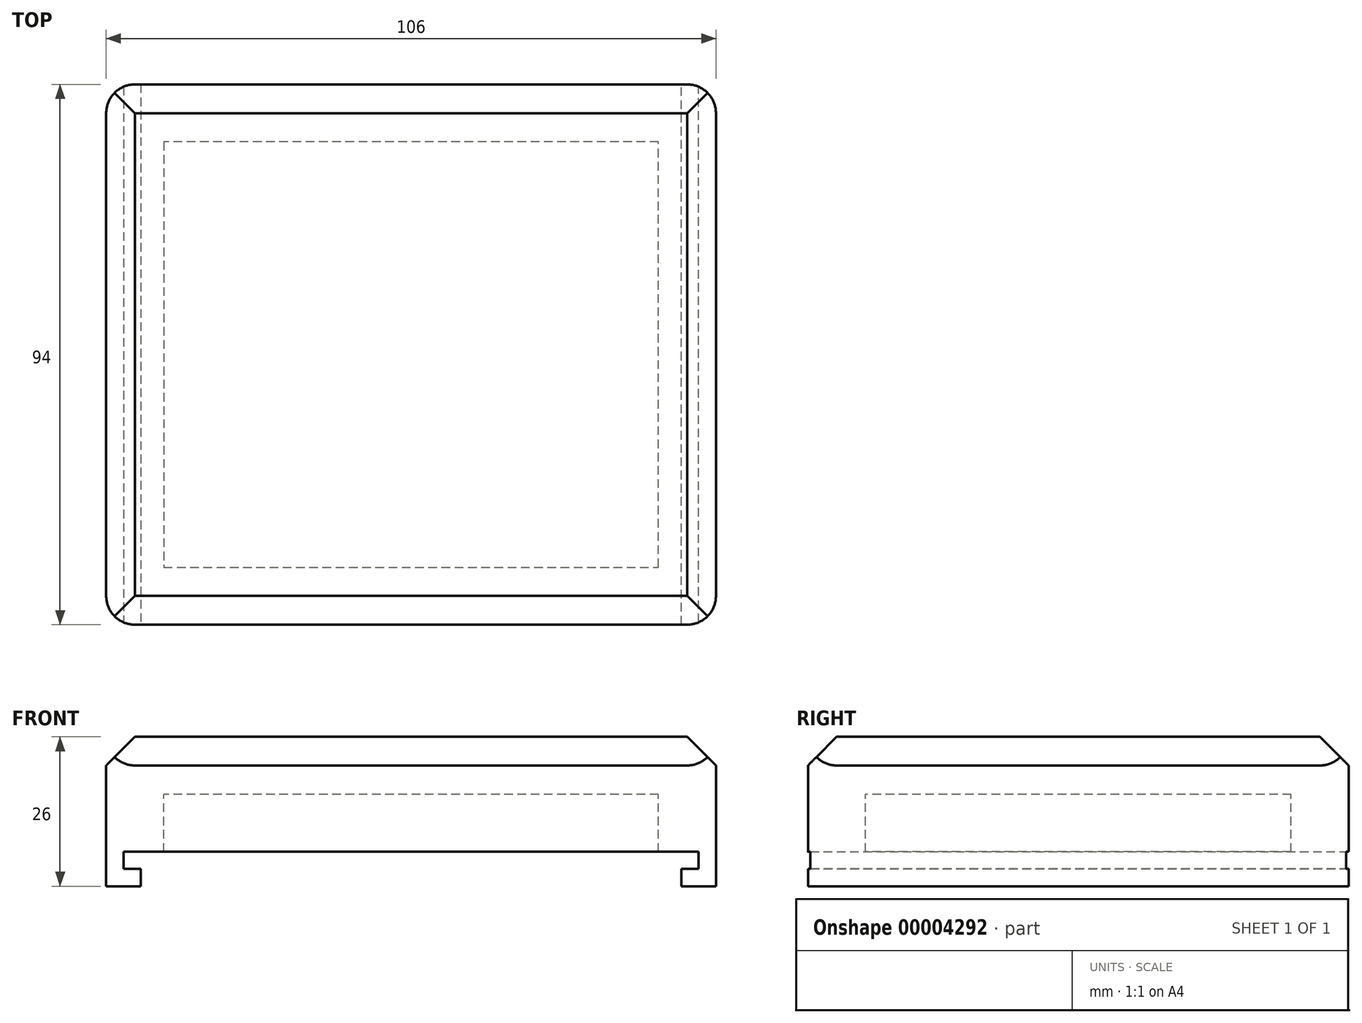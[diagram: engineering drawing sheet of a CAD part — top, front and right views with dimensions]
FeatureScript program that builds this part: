
annotation { "Feature Type Name" : "Feature", "Feature Type Description" : "" }
export const myFeature = defineFeature(function(context is Context, id is Id, definition is map)
    precondition{}
    {
        {
            var Q0;
            Q0=qCreatedBy(makeId("Top.planeOp"),FACE);
            var sketch = newSketch(context, id + "F0", { "sketchPlane" : qUnion([Q0])});
            skLineSegment(sketch, "E0", {"start": v(-102.5, 83.2) * mm, "end": v(-208.5, 83.2) * mm});
            skLineSegment(sketch, "E1", {"start": v(-208.5, 83.2) * mm, "end": v(-208.5, -10.8) * mm});
            skLineSegment(sketch, "E2", {"start": v(-208.5, -10.8) * mm, "end": v(-102.5, -10.8) * mm});
            skLineSegment(sketch, "E3", {"start": v(-102.5, -10.8) * mm, "end": v(-102.5, 83.2) * mm});
            skSolve(sketch);
        }
        {
            var Q0;
            Q0=makeQuery(id+"F0.imprint","IMPRINT",FACE,{"disambiguationData":[TD([[makeQuery(id+"F0.imprint","IMPRINT",EDGE,{"derivedFrom":sQuery(id+"F0.wireOp",EDGE,"E0")}),1.0]])]});
            extrude(context, id + "F1", {"entities" : qUnion([Q0]), "depth" : 10 * mm});
        }
        {
            var Q0;
            Q0=makeQuery(id+"F1.opExtrude","CAP_FACE",FACE,{"disambiguationData":[OSD([sQuery(id+"F0.wireOp",EDGE,"E0"),sQuery(id+"F0.wireOp",EDGE,"E1"),sQuery(id+"F0.wireOp",EDGE,"E2"),sQuery(id+"F0.wireOp",EDGE,"E3")])],"isStart":true});
            var sketch = newSketch(context, id + "F2", { "sketchPlane" : qUnion([Q0])});
            skSolve(sketch);
        }
        {
            var Q0;
            Q0=makeQuery(id+"F2.imprint","IMPRINT",FACE,{"disambiguationData":[TD([[makeQuery(id+"F2.imprint","IMPRINT",EDGE,{"derivedFrom":makeQuery(id+"F1.opExtrude","CAP_EDGE",EDGE,{"disambiguationData":[OSD([sQuery(id+"F0.wireOp",EDGE,"E0")])],"isStart":true})}),-1.0]])]});
            var sketch = newSketch(context, id + "F3", { "sketchPlane" : qUnion([Q0])});
            skLineSegment(sketch, "E4.0", {"start": v(-198.5, -73.2) * mm, "end": v(-198.5, 0.8) * mm});
            skLineSegment(sketch, "E4.1", {"start": v(-112.5, -73.2) * mm, "end": v(-198.5, -73.2) * mm});
            skLineSegment(sketch, "E4.2", {"start": v(-112.5, 0.8) * mm, "end": v(-112.5, -73.2) * mm});
            skLineSegment(sketch, "E4.3", {"start": v(-198.5, 0.8) * mm, "end": v(-112.5, 0.8) * mm});
            skSolve(sketch);
        }
        {
            var Q0;
            Q0=makeQuery(id+"F3.imprint","IMPRINT",FACE,{"disambiguationData":[TD([[makeQuery(id+"F3.imprint","IMPRINT",EDGE,{"derivedFrom":sQuery(id+"F3.wireOp",EDGE,"E4.0")}),1.0]])]});
            extrude(context, id + "F4", {"entities" : qUnion([Q0]), "operationType" : NewBodyOperationType.ADD, "depth" : 10 * mm});
        }
        {
            var Q0;
            Q0=makeQuery(id+"F4.opExtrude","CAP_FACE",FACE,{"disambiguationData":[OSD([sQuery(id+"F0.wireOp",EDGE,"E0"),sQuery(id+"F0.wireOp",EDGE,"E1"),sQuery(id+"F0.wireOp",EDGE,"E2"),sQuery(id+"F0.wireOp",EDGE,"E3"),sQuery(id+"F3.wireOp",EDGE,"E4.0"),sQuery(id+"F3.wireOp",EDGE,"E4.1"),sQuery(id+"F3.wireOp",EDGE,"E4.2"),sQuery(id+"F3.wireOp",EDGE,"E4.3")])],"isStart":false});
            var sketch = newSketch(context, id + "F5", { "sketchPlane" : qUnion([Q0])});
            skLineSegment(sketch, "E5.0", {"start": v(-205.5, -83.2) * mm, "end": v(-205.5, 10.8) * mm});
            skLineSegment(sketch, "E6.0", {"start": v(-105.5, 10.8) * mm, "end": v(-105.5, -83.2) * mm});
            skSolve(sketch);
        }
        {
            var Q0;
            {var subQ1=sQuery(id+"F5.wireOp",EDGE,"E5.0");Q0=makeQuery(id+"F5.imprint","IMPRINT",FACE,{"disambiguationData":[TD([[makeQuery(id+"F5.imprint","IMPRINT",EDGE,{"derivedFrom":subQ1}),1.0]])]});}
            var Q1;
            {var subQ1=sQuery(id+"F5.wireOp",EDGE,"E6.0");Q1=makeQuery(id+"F5.imprint","IMPRINT",FACE,{"disambiguationData":[TD([[makeQuery(id+"F5.imprint","IMPRINT",EDGE,{"derivedFrom":subQ1}),1.0]])]});}
            extrude(context, id + "F6", {"entities" : qUnion([Q0, Q1]), "operationType" : NewBodyOperationType.ADD, "depth" : 6 * mm});
        }
        {
            var Q0;
            Q0=makeQuery(id+"F6.opExtrude","SWEPT_FACE",FACE,{"disambiguationData":[OSD([sQuery(id+"F5.wireOp",EDGE,"E5.0")])]});
            var sketch = newSketch(context, id + "F7", { "sketchPlane" : qUnion([Q0])});
            skLineSegment(sketch, "E7.0", {"start": v(83.2, -13) * mm, "end": v(-10.8, -13) * mm});
            skSolve(sketch);
        }
        {
            var Q0;
            {var subQ2=sQuery(id+"F7.wireOp",EDGE,"E7.0");Q0=makeQuery(id+"F7.imprint","IMPRINT",FACE,{"disambiguationData":[TD([[makeQuery(id+"F7.imprint","IMPRINT",EDGE,{"derivedFrom":subQ2}),1.0]])]});}
            extrude(context, id + "F8", {"entities" : qUnion([Q0]), "operationType" : NewBodyOperationType.ADD, "depth" : 3 * mm});
        }
        {
            var Q0;
            Q0=makeQuery(id+"F6.opExtrude","SWEPT_FACE",FACE,{"disambiguationData":[OSD([sQuery(id+"F5.wireOp",EDGE,"E6.0")])]});
            var sketch = newSketch(context, id + "F9", { "sketchPlane" : qUnion([Q0])});
            skLineSegment(sketch, "E8.0", {"start": v(10.8, -13) * mm, "end": v(-83.2, -13) * mm});
            skSolve(sketch);
        }
        {
            var Q0;
            {var subQ2=sQuery(id+"F9.wireOp",EDGE,"E8.0");Q0=makeQuery(id+"F9.imprint","IMPRINT",FACE,{"disambiguationData":[TD([[makeQuery(id+"F9.imprint","IMPRINT",EDGE,{"derivedFrom":subQ2}),1.0]])]});}
            extrude(context, id + "F10", {"entities" : qUnion([Q0]), "operationType" : NewBodyOperationType.ADD, "depth" : 3 * mm});
        }
        {
            var Q0;
            Q0=makeQuery(id+"F1.opExtrude","CAP_EDGE",EDGE,{"disambiguationData":[OSD([sQuery(id+"F0.wireOp",EDGE,"E2")])],"isStart":false});
            var Q1;
            Q1=makeQuery(id+"F1.opExtrude","CAP_EDGE",EDGE,{"disambiguationData":[OSD([sQuery(id+"F0.wireOp",EDGE,"E1")])],"isStart":false});
            var Q2;
            Q2=makeQuery(id+"F1.opExtrude","CAP_EDGE",EDGE,{"disambiguationData":[OSD([sQuery(id+"F0.wireOp",EDGE,"E0")])],"isStart":false});
            var Q3;
            Q3=makeQuery(id+"F1.opExtrude","CAP_EDGE",EDGE,{"disambiguationData":[OSD([sQuery(id+"F0.wireOp",EDGE,"E3")])],"isStart":false});
            chamfer(context, id + "F11", {"entities" : qUnion([Q0, Q1, Q2, Q3]), "width" : 5 * mm, "tangentPropagation" : true});
        }
        {
            var Q0;
            {var subQ0=sQuery(id+"F0.wireOp",EDGE,"E0");var subQ1=sQuery(id+"F0.wireOp",EDGE,"E1");Q0=makeQuery(id+"F6.boolean.opBoolean","MERGE",EDGE,{"derivedFrom":[makeQuery(id+"F4.boolean.opBoolean","MERGE",EDGE,{"derivedFrom":[makeQuery(id+"F1.opExtrude","SWEPT_EDGE",EDGE,{"disambiguationData":[OSD([subQ0,subQ1])]}),makeQuery(id+"F4.opExtrude","SWEPT_EDGE",EDGE,{"disambiguationData":[OSD([subQ0,subQ1])]})]}),makeQuery(id+"F6.opExtrude","SWEPT_EDGE",EDGE,{"disambiguationData":[OSD([subQ0,subQ1])]})]});}
            var Q1;
            {var subQ0=sQuery(id+"F0.wireOp",EDGE,"E1");var subQ1=sQuery(id+"F0.wireOp",EDGE,"E2");Q1=makeQuery(id+"F6.boolean.opBoolean","MERGE",EDGE,{"derivedFrom":[makeQuery(id+"F4.boolean.opBoolean","MERGE",EDGE,{"derivedFrom":[makeQuery(id+"F1.opExtrude","SWEPT_EDGE",EDGE,{"disambiguationData":[OSD([subQ0,subQ1])]}),makeQuery(id+"F4.opExtrude","SWEPT_EDGE",EDGE,{"disambiguationData":[OSD([subQ0,subQ1])]})]}),makeQuery(id+"F6.opExtrude","SWEPT_EDGE",EDGE,{"disambiguationData":[OSD([subQ0,subQ1])]})]});}
            var Q2;
            {var subQ0=sQuery(id+"F0.wireOp",EDGE,"E2");var subQ1=sQuery(id+"F0.wireOp",EDGE,"E3");Q2=makeQuery(id+"F6.boolean.opBoolean","MERGE",EDGE,{"derivedFrom":[makeQuery(id+"F4.boolean.opBoolean","MERGE",EDGE,{"derivedFrom":[makeQuery(id+"F1.opExtrude","SWEPT_EDGE",EDGE,{"disambiguationData":[OSD([subQ0,subQ1])]}),makeQuery(id+"F4.opExtrude","SWEPT_EDGE",EDGE,{"disambiguationData":[OSD([subQ0,subQ1])]})]}),makeQuery(id+"F6.opExtrude","SWEPT_EDGE",EDGE,{"disambiguationData":[OSD([subQ0,subQ1])]})]});}
            var Q3;
            {var subQ0=sQuery(id+"F0.wireOp",EDGE,"E0");var subQ1=sQuery(id+"F0.wireOp",EDGE,"E3");Q3=makeQuery(id+"F6.boolean.opBoolean","MERGE",EDGE,{"derivedFrom":[makeQuery(id+"F4.boolean.opBoolean","MERGE",EDGE,{"derivedFrom":[makeQuery(id+"F1.opExtrude","SWEPT_EDGE",EDGE,{"disambiguationData":[OSD([subQ0,subQ1])]}),makeQuery(id+"F4.opExtrude","SWEPT_EDGE",EDGE,{"disambiguationData":[OSD([subQ0,subQ1])]})]}),makeQuery(id+"F6.opExtrude","SWEPT_EDGE",EDGE,{"disambiguationData":[OSD([subQ0,subQ1])]})]});}
            fillet(context, id + "F12", {"entities" : qUnion([Q0, Q1, Q2, Q3]), "radius" : 5 * mm, "tangentPropagation" : true, "allowEdgeOverflow" : false});
        }
    });
